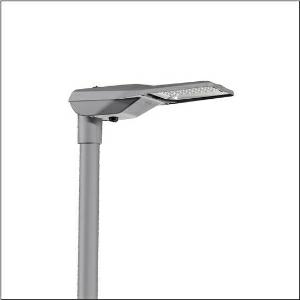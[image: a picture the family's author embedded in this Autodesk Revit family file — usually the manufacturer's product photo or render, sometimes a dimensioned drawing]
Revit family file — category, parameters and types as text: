
# Revit family: streetlight_sl_21_mini___stw1_0a_5xe2e43t08jb_eeda
name_source: partatom
category: Lighting Fixtures
units: mm (PartAtom-declared; Revit-internal decimal feet)

## family parameters
Cut with Voids When Loaded = No
Host = Face
Light Source = No
Part Type = Normal
Room Calculation Point = No
Round Connector Dimension = Use Diameter
Shared = No

## types (1)
- --- (1 x LED, 13500 lm, 88.6 W, 4000K)
    Apparent Load = 89 VA
    CIE Flux Codes = 39 75 98 100 100
    Color Rendering = 70
    Color Temperature = 4000K
    Default Elevation = 1800 mm
    Description = Streetlight SL 21 mini, mast luminaire, primary light control with lens, of PMMA, primary optical cover: cover, of toughened safety glass, transparent, light distribution: STW1.0a, light emission: direct distribution, primary light characteristic: asymmetric, installation type: side-entry, post-top, LED, High Power LED, rated luminous flux: 13.500lm, luminous efficacy: 152lm/W, light colour: 740, colour temperature: 4000K, control gear: D4i, control: overheat protection, constant luminous flux control, time-dependent luminous flux control, flexible luminous flux parameterisation, pre-setting: logarithmic dimming characteristic, mains connection: 220..240V, AC, 50/60Hz, start of lifetime: 89W, end of service life: 92W, reduction: 41W, luminaire housing, of diecast aluminium, powder-coated, SITECO metallic grey (DB 702S), corrosivity category C5 high according to DIN EN ISO 12944, please order mast flange separately, inclination adjustable: 0°, 5°, 10°, 15°, sealing non-destructively replaceable, multi-level sealing system, length: 628mm, width: 235mm, height: 110mm, mast flange for spigot size: 42mm (side-entry): 5XC10008XM4, 60/48mm (side-entry/post-top): 5XC10108XM2, 76/60mm (side-entry/post-top): 5XC10108XM1, mounting height: 4..8m, Smart Interface below and above, protection rating (complete): IP66, insulation class (complete): insulation class II (safety insulation), certification: CE, ENEC, ENEC+, VDE, impact resistance: IK10, permissible operating ambient temperature for outdoor applications: -40..+50°C, standard-compliant lighting for roads and squares, packaging unit: 1 piece

Light Distribution: STW1.0a
    Height = 110 mm
    Lamp = 1 x LED
    Lamp Light Flux = 13500 lm
    Lamp Power = 88.6 W
    Lamp count = 1
    Length = 625 mm
    Luminous efficacy = 152 lm/W
    Manufacturer = Siteco
    ModVariant = No
    Model = 5XE2E43T08JB
    Number of Poles = 1
    OnlyDefault = Yes
    Power Factor = 1
    Product Name = Streetlight SL 21 mini | STW1.0a
    Product group = mast luminaire | pylon top
    ProductGroupID = 6100
    Protection Class = Protection class II
    Protection Degree = IP 66
    RLX_Detail_Level = 1
    RLX_Emergency_Light_Flux = 0 lm
    RLX_Emergency_Type = 0
    RLX_Emergency_Type_DB = No
    RlxData = <blob elided: 26453 chars, md5=08c62b1f>
    Socket = socket
    Standby Power = 0 W
    System Light Flux = 13500 lm
    System Power = 89 W
    Type Comments = factory setting: luminous flux: 100 % | dim-lin: 254 | 915 mA
    Type Image = l_1003514.jpg
    URL = http://relux.com
    VarID = @adj_031159
    Voltage = 0 V
    Weight = 0.00 kg
    Width = 234 mm

## geometry (parser evidence)
native form markers: Blend x4, Sweep x10
no freeform markers — native parametric forms only
